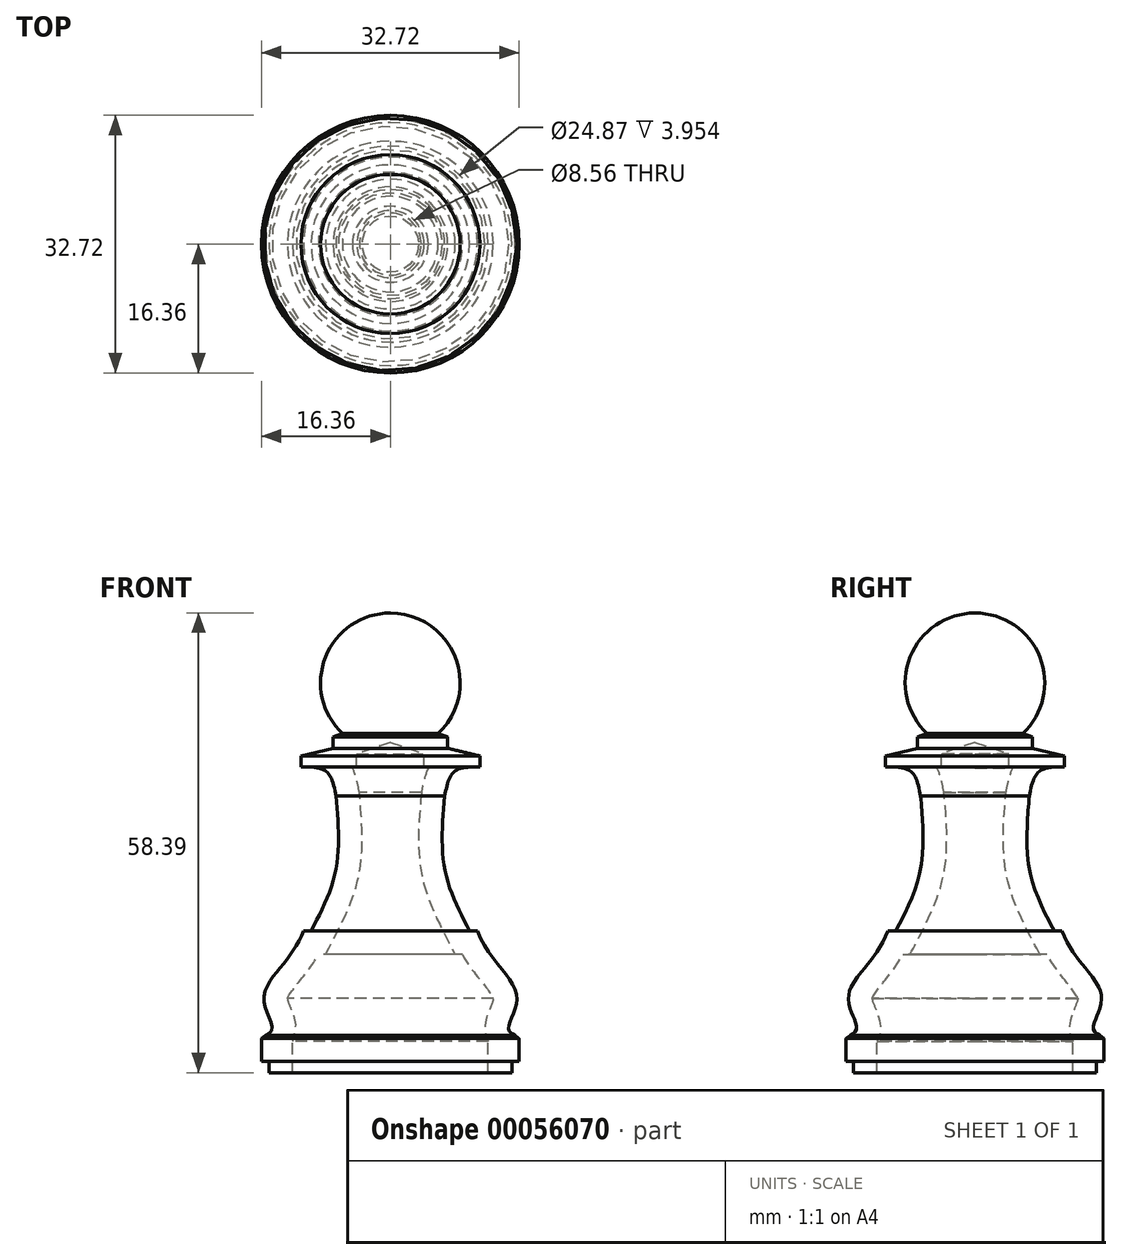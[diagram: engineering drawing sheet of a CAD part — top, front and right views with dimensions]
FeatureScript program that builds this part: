
annotation { "Feature Type Name" : "Feature", "Feature Type Description" : "" }
export const myFeature = defineFeature(function(context is Context, id is Id, definition is map)
    precondition{}
    {
        {
            var Q0;
            Q0=qCreatedBy(makeId("Front.planeOp"),FACE);
            var sketch = newSketch(context, id + "F0", { "sketchPlane" : qUnion([Q0])});
            skLineSegment(sketch, "E0", {"start": v(81.65, -16.9) * mm, "end": v(82.66, -74.9) * mm});
            skLineSegment(sketch, "E1", {"start": v(0, 48.24) * mm, "end": v(0, -40.92) * mm, "construction": true});
            skArc(sketch, "E2", {"start": v(6.07, 18.06) * mm, "mid": v(8.24, 27.8) * mm, "end": v(0, 33.4) * mm});
            skLineSegment(sketch, "E3", {"start": v(6.07, 18.06) * mm, "end": v(7.28, 17.65) * mm});
            skLineSegment(sketch, "E4", {"start": v(7.28, 17.65) * mm, "end": v(7.28, 16.2) * mm});
            skLineSegment(sketch, "E5", {"start": v(15.84, -20.27) * mm, "end": v(16.36, -20.67) * mm});
            skLineSegment(sketch, "E6", {"start": v(16.36, -20.67) * mm, "end": v(16.36, -23.56) * mm});
            skLineSegment(sketch, "E7", {"start": v(16.36, -23.56) * mm, "end": v(15.43, -23.56) * mm});
            skLineSegment(sketch, "E8", {"start": v(15.43, -23.56) * mm, "end": v(15.43, -25) * mm});
            skLineSegment(sketch, "E9", {"start": v(7.28, 16.2) * mm, "end": v(11.36, 15.24) * mm});
            skLineSegment(sketch, "E10", {"start": v(11.36, 15.24) * mm, "end": v(11.36, 13.87) * mm});
            skFitSpline(sketch, "E11", {"points": [v(11.36, 13.87) * mm, v(8.13, 13.23) * mm, v(6.91, 10.16) * mm], "startDerivative": vector(-7.47, -0.06) * mm, "endDerivative": vector(-1.42, -7.35) * mm});
            skFitSpline(sketch, "E12", {"points": [v(6.91, 10.16) * mm, v(6.91, 0.81) * mm, v(10.06, -7) * mm], "startDerivative": vector(-1.66, -18.79) * mm, "endDerivative": vector(8.04, -15.52) * mm});
            skLineSegment(sketch, "E13", {"start": v(10.06, -7) * mm, "end": v(11.04, -7) * mm});
            skFitSpline(sketch, "E14", {"points": [v(11.04, -7) * mm, v(16.06, -15.3) * mm, v(15.01, -19.35) * mm, v(15.84, -20.27) * mm], "startDerivative": vector(8.5, -22.67) * mm, "endDerivative": vector(7.23, -4.2) * mm});
            skLineSegment(sketch, "E15", {"start": v(15.43, -25) * mm, "end": v(0, -25) * mm});
            skLineSegment(sketch, "E16", {"start": v(0, 33.4) * mm, "end": v(0, -25) * mm});
            skSolve(sketch);
        }
        {
            var Q0;
            Q0=makeQuery(id+"F0.imprint","IMPRINT",FACE,{"disambiguationData":[TD([[makeQuery(id+"F0.imprint","IMPRINT",EDGE,{"derivedFrom":sQuery(id+"F0.wireOp",EDGE,"E2")}),1.0]])]});
            var Q1;
            Q1=sQuery(id+"F0.wireOp",EDGE,"E16");
            revolve(context, id + "F1", {"entities" : qUnion([Q0]), "axis" : qUnion([Q1]), "revolveType" : RevolveType.FULL});
        }
        {
            var Q0;
            Q0=makeQuery(id+"F1.opRevolve","SWEPT_FACE",FACE,{"disambiguationData":[OSD([sQuery(id+"F0.wireOp",EDGE,"E15")])]});
            shell(context, id + "F2", {"entities" : qUnion([Q0]), "thickness" : 3 * mm});
        }
    });
